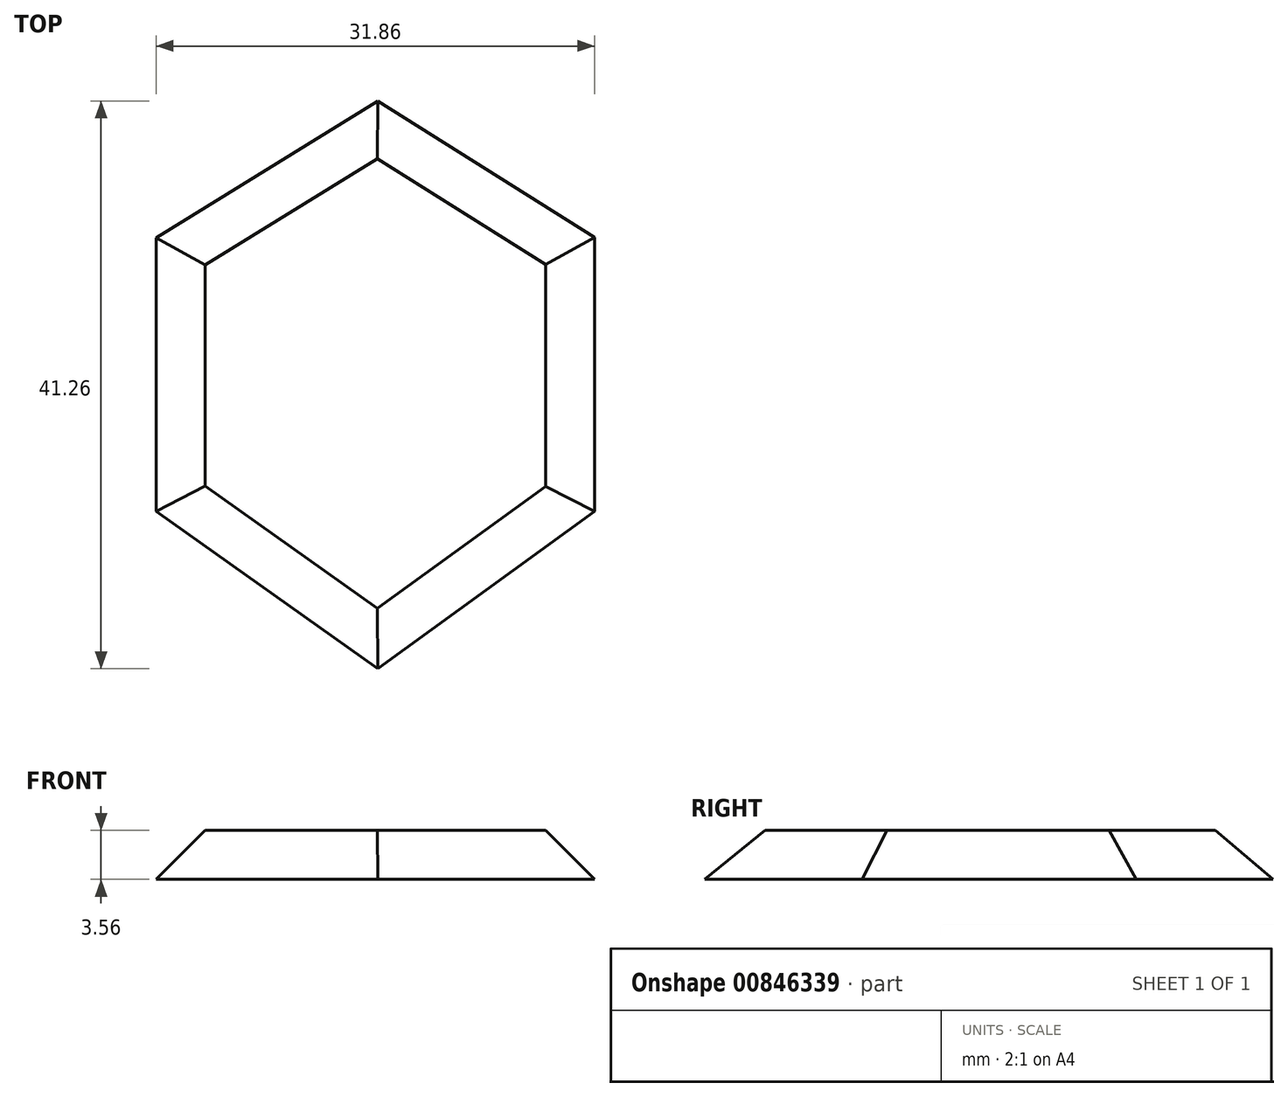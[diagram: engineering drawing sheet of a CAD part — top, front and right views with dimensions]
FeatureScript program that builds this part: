
annotation { "Feature Type Name" : "Feature", "Feature Type Description" : "" }
export const myFeature = defineFeature(function(context is Context, id is Id, definition is map)
    precondition{}
    {
        {
            var Q0;
            Q0=qCreatedBy(makeId("Top.planeOp"),FACE);
            var sketch = newSketch(context, id + "F0", { "sketchPlane" : qUnion([Q0])});
            skLineSegment(sketch, "E0", {"start": v(0, 0) * mm, "end": v(-17.62, 12.52) * mm});
            skLineSegment(sketch, "E1", {"start": v(0, 0) * mm, "end": v(17.28, 12.52) * mm});
            skLineSegment(sketch, "E2", {"start": v(-17.62, 12.52) * mm, "end": v(-17.62, 34.06) * mm});
            skLineSegment(sketch, "E3", {"start": v(17.28, 12.52) * mm, "end": v(17.28, 34.06) * mm});
            skLineSegment(sketch, "E4", {"start": v(17.28, 34.06) * mm, "end": v(17.28, 34.06) * mm});
            skLineSegment(sketch, "E5", {"start": v(-17.62, 34.06) * mm, "end": v(0, 44.93) * mm});
            skLineSegment(sketch, "E6", {"start": v(0, 44.93) * mm, "end": v(17.28, 34.06) * mm});
            skSolve(sketch);
        }
        {
            var Q0;
            Q0=makeQuery(id+"F0.imprint","IMPRINT",FACE,{"disambiguationData":[TD([[makeQuery(id+"F0.imprint","IMPRINT",EDGE,{"derivedFrom":sQuery(id+"F0.wireOp",EDGE,"E0")}),-1.0]])]});
            extrude(context, id + "F1", {"entities" : qUnion([Q0]), "depth" : 0.5 * mm, "offsetDistance" : 25.4 * mm});
        }
        {
            var Q0;
            Q0=makeQuery(id+"F1.opExtrude","CAP_FACE",FACE,{"disambiguationData":[OSD([sQuery(id+"F0.wireOp",EDGE,"E0"),sQuery(id+"F0.wireOp",EDGE,"E1"),sQuery(id+"F0.wireOp",EDGE,"E2"),sQuery(id+"F0.wireOp",EDGE,"E3"),sQuery(id+"F0.wireOp",EDGE,"E5"),sQuery(id+"F0.wireOp",EDGE,"E6")])],"isStart":false});
            extrude(context, id + "F2", {"entities" : qUnion([Q0]), "operationType" : NewBodyOperationType.ADD, "depth" : 3.05 * mm, "offsetDistance" : 25.4 * mm});
        }
        {
            var Q0;
            Q0=makeQuery(id+"F2.opExtrude","CAP_FACE",FACE,{"disambiguationData":[OSD([sQuery(id+"F0.wireOp",EDGE,"E0"),sQuery(id+"F0.wireOp",EDGE,"E1"),sQuery(id+"F0.wireOp",EDGE,"E2"),sQuery(id+"F0.wireOp",EDGE,"E3"),sQuery(id+"F0.wireOp",EDGE,"E5"),sQuery(id+"F0.wireOp",EDGE,"E6")])],"isStart":false});
            chamfer(context, id + "F3", {"entities" : qUnion([Q0]), "width" : 5.08 * mm, "tangentPropagation" : true});
        }
    });
